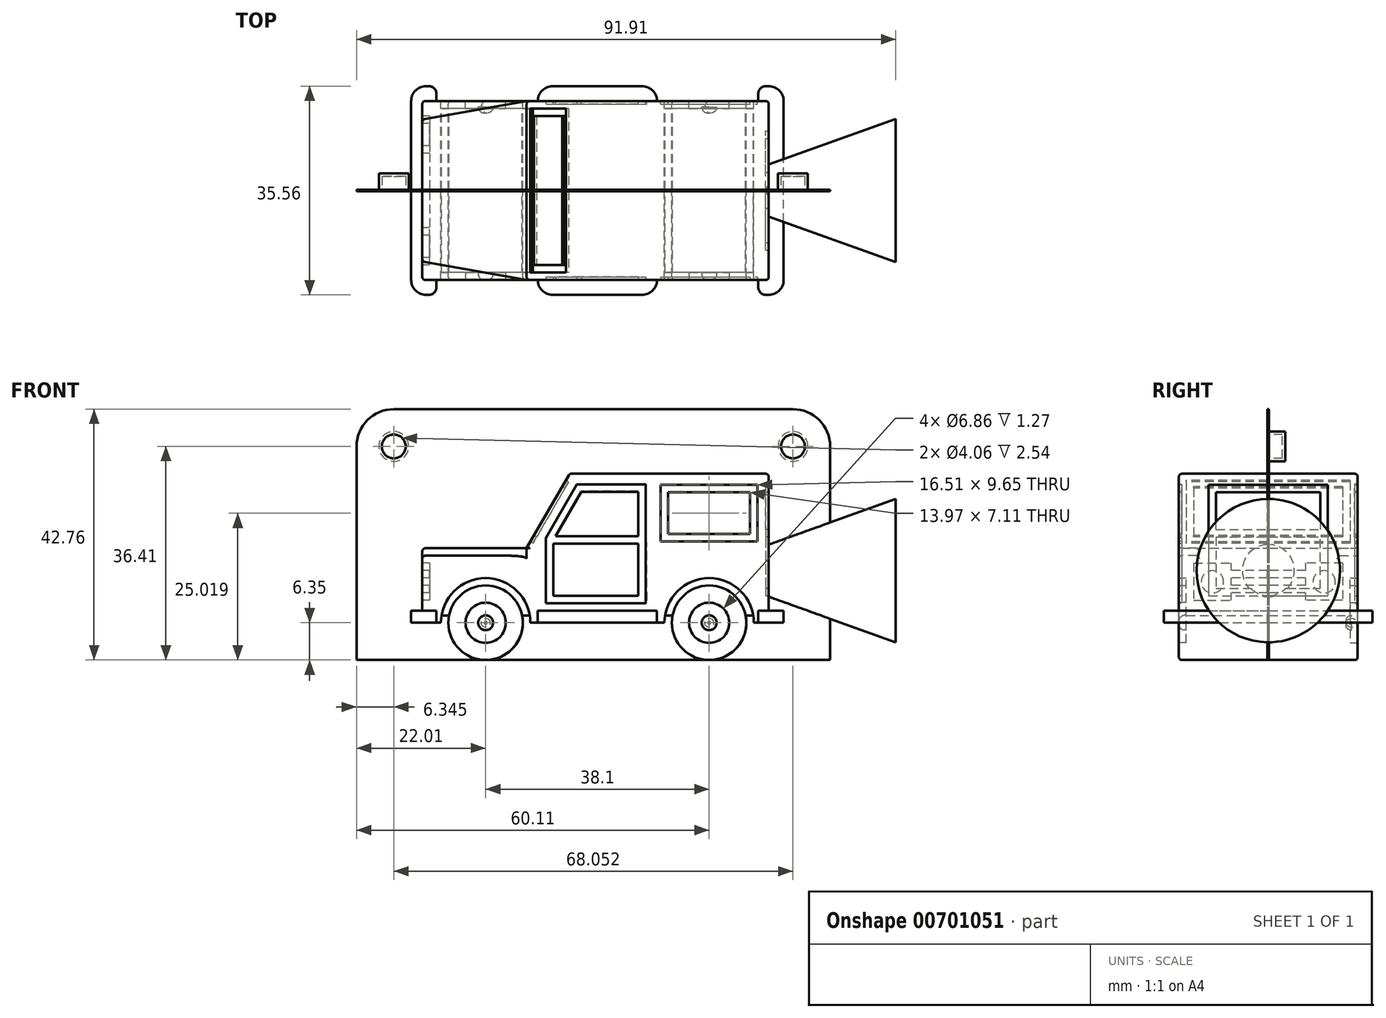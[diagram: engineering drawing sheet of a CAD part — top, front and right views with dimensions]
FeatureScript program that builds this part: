
annotation { "Feature Type Name" : "Feature", "Feature Type Description" : "" }
export const myFeature = defineFeature(function(context is Context, id is Id, definition is map)
    precondition{}
    {
        {
            var Q0;
            Q0=qCreatedBy(makeId("Front.planeOp"),FACE);
            var sketch = newSketch(context, id + "F0", { "sketchPlane" : qUnion([Q0])});
            skLineSegment(sketch, "E0", {"start": v(-29.85, 6.35) * mm, "end": v(42.48, 6.35) * mm, "construction": true});
            skPoint(sketch, "E1", {"position": v(-19.05, 6.35) * mm});
            skPoint(sketch, "E2", {"position": v(19.05, 6.35) * mm});
            skLineSegment(sketch, "E3", {"start": v(-105.53, 0) * mm, "end": v(109.36, 0) * mm, "construction": true});
            skCircle(sketch, "E4", {"center": v(-19.05, 6.35) * mm, "radius": 6.35 * mm});
            skCircle(sketch, "E5", {"center": v(19.05, 6.35) * mm, "radius": 6.35 * mm});
            skArc(sketch, "E6", {"start": v(-11.43, 6.35) * mm, "mid": v(-19.05, 13.97) * mm, "end": v(-26.67, 6.35) * mm});
            skArc(sketch, "E7", {"start": v(26.67, 6.35) * mm, "mid": v(19.05, 13.97) * mm, "end": v(11.43, 6.35) * mm});
            skLineSegment(sketch, "E8", {"start": v(-26.67, 6.35) * mm, "end": v(-29.85, 6.35) * mm});
            skLineSegment(sketch, "E9", {"start": v(-29.85, 19.05) * mm, "end": v(-12.07, 19.05) * mm});
            skLineSegment(sketch, "E10", {"start": v(-12.07, 19.05) * mm, "end": v(-4.73, 31.75) * mm});
            skLineSegment(sketch, "E11", {"start": v(-4.73, 31.75) * mm, "end": v(29.21, 31.75) * mm});
            skLineSegment(sketch, "E12", {"start": v(29.21, 31.75) * mm, "end": v(29.21, 6.35) * mm});
            skLineSegment(sketch, "E13", {"start": v(29.21, 6.35) * mm, "end": v(26.67, 6.35) * mm});
            skLineSegment(sketch, "E14", {"start": v(11.43, 6.35) * mm, "end": v(-11.43, 6.35) * mm});
            skLineSegment(sketch, "E15", {"start": v(-29.85, 19.05) * mm, "end": v(-29.85, 6.35) * mm});
            skSolve(sketch);
        }
        {
            var Q0;
            Q0=makeQuery(id+"F0.imprint","IMPRINT",FACE,{"disambiguationData":[TD([[makeQuery(id+"F0.imprint","IMPRINT",EDGE,{"derivedFrom":sQuery(id+"F0.wireOp",EDGE,"E6")}),-1.0]])]});
            var Q1;
            Q1=makeQuery(id+"F0.imprint","IMPRINT",FACE,{"disambiguationData":[TD([[makeQuery(id+"F0.imprint","IMPRINT",EDGE,{"derivedFrom":sQuery(id+"F0.wireOp",EDGE,"E4")}),1.0]])]});
            var Q2;
            Q2=makeQuery(id+"F0.imprint","IMPRINT",FACE,{"disambiguationData":[TD([[makeQuery(id+"F0.imprint","IMPRINT",EDGE,{"derivedFrom":sQuery(id+"F0.wireOp",EDGE,"E5")}),1.0]])]});
            extrude(context, id + "F1", {"entities" : qUnion([Q0, Q1, Q2]), "endBound" : BoundingType.SYMMETRIC, "depth" : 30.48 * mm, "offsetDistance" : 25.4 * mm});
        }
        {
            var Q0;
            Q0=makeQuery(id+"F1.opExtrude","SWEPT_FACE",FACE,{"disambiguationData":[OSD([sQuery(id+"F0.wireOp",EDGE,"E14")])]});
            var sketch = newSketch(context, id + "F2", { "sketchPlane" : qUnion([Q0])});
            skLineSegment(sketch, "E16.bottom", {"start": v(-7.62, 17.78) * mm, "end": v(7.62, 17.78) * mm});
            skLineSegment(sketch, "E16.top", {"start": v(-7.62, -17.78) * mm, "end": v(7.62, -17.78) * mm});
            skLineSegment(sketch, "E16.left", {"start": v(-10.16, 15.24) * mm, "end": v(-10.16, -15.24) * mm});
            skLineSegment(sketch, "E16.right", {"start": v(10.16, 15.24) * mm, "end": v(10.16, -15.24) * mm});
            skPoint(sketch, "E17.visualSharp", {"position": v(-10.16, 17.78) * mm});
            skArc(sketch, "E17.filletArc", {"start": v(-7.62, 17.78) * mm, "mid": v(-9.42, 17.04) * mm, "end": v(-10.16, 15.24) * mm});
            skPoint(sketch, "E18.visualSharp", {"position": v(10.16, 17.78) * mm});
            skArc(sketch, "E18.filletArc", {"start": v(10.16, 15.24) * mm, "mid": v(9.42, 17.04) * mm, "end": v(7.62, 17.78) * mm});
            skPoint(sketch, "E19.visualSharp", {"position": v(10.16, -17.78) * mm});
            skArc(sketch, "E19.filletArc", {"start": v(7.62, -17.78) * mm, "mid": v(9.42, -17.04) * mm, "end": v(10.16, -15.24) * mm});
            skPoint(sketch, "E20.visualSharp", {"position": v(-10.16, -17.78) * mm});
            skArc(sketch, "E20.filletArc", {"start": v(-10.16, -15.24) * mm, "mid": v(-9.42, -17.04) * mm, "end": v(-7.62, -17.78) * mm});
            skLineSegment(sketch, "E21.bottom", {"start": v(-29.21, 17.78) * mm, "end": v(-28.7, 17.78) * mm});
            skLineSegment(sketch, "E21.top", {"start": v(-29.21, -17.78) * mm, "end": v(-28.7, -17.78) * mm});
            skLineSegment(sketch, "E21.left", {"start": v(-31.75, 15.24) * mm, "end": v(-31.75, -15.24) * mm});
            skLineSegment(sketch, "E21.right", {"start": v(-27.43, 16.51) * mm, "end": v(-27.43, -16.51) * mm});
            skPoint(sketch, "E22.visualSharp", {"position": v(-31.75, 17.78) * mm});
            skArc(sketch, "E22.filletArc", {"start": v(-29.21, 17.78) * mm, "mid": v(-31, 17.04) * mm, "end": v(-31.75, 15.24) * mm});
            skPoint(sketch, "E23.visualSharp", {"position": v(-31.75, -17.78) * mm});
            skArc(sketch, "E23.filletArc", {"start": v(-31.75, -15.24) * mm, "mid": v(-31, -17.04) * mm, "end": v(-29.21, -17.78) * mm});
            skPoint(sketch, "E24.visualSharp", {"position": v(-27.43, 17.78) * mm});
            skArc(sketch, "E24.filletArc", {"start": v(-27.43, 16.51) * mm, "mid": v(-27.8, 17.4) * mm, "end": v(-28.7, 17.78) * mm});
            skPoint(sketch, "E25.visualSharp", {"position": v(-27.43, -17.78) * mm});
            skArc(sketch, "E25.filletArc", {"start": v(-28.7, -17.78) * mm, "mid": v(-27.8, -17.4) * mm, "end": v(-27.43, -16.51) * mm});
            skLineSegment(sketch, "E26.bottom", {"start": v(28.7, 17.78) * mm, "end": v(29.21, 17.78) * mm});
            skLineSegment(sketch, "E26.top", {"start": v(28.7, -17.78) * mm, "end": v(29.21, -17.78) * mm});
            skLineSegment(sketch, "E26.left", {"start": v(27.43, 16.51) * mm, "end": v(27.43, -16.51) * mm});
            skLineSegment(sketch, "E26.right", {"start": v(31.75, 15.24) * mm, "end": v(31.75, -15.24) * mm});
            skPoint(sketch, "E27.visualSharp", {"position": v(27.43, 17.78) * mm});
            skArc(sketch, "E27.filletArc", {"start": v(28.7, 17.78) * mm, "mid": v(27.8, 17.4) * mm, "end": v(27.43, 16.51) * mm});
            skPoint(sketch, "E28.visualSharp", {"position": v(27.43, -17.78) * mm});
            skArc(sketch, "E28.filletArc", {"start": v(27.43, -16.51) * mm, "mid": v(27.8, -17.4) * mm, "end": v(28.7, -17.78) * mm});
            skPoint(sketch, "E29.visualSharp", {"position": v(31.75, 17.78) * mm});
            skArc(sketch, "E29.filletArc", {"start": v(31.75, 15.24) * mm, "mid": v(31, 17.04) * mm, "end": v(29.21, 17.78) * mm});
            skPoint(sketch, "E30.visualSharp", {"position": v(31.75, -17.78) * mm});
            skArc(sketch, "E30.filletArc", {"start": v(29.21, -17.78) * mm, "mid": v(31, -17.04) * mm, "end": v(31.75, -15.24) * mm});
            skSolve(sketch);
        }
        {
            var Q0;
            Q0 = qSketchRegion(id + "F2", true);
            extrude(context, id + "F3", {"entities" : qUnion([Q0]), "operationType" : NewBodyOperationType.ADD, "oppositeDirection" : true, "depth" : 2.03 * mm, "offsetDistance" : 25.4 * mm});
        }
        {
            var Q0;
            Q0=qCreatedBy(makeId("Front.planeOp"),FACE);
            var sketch = newSketch(context, id + "F4", { "sketchPlane" : qUnion([Q0])});
            skLineSegment(sketch, "E31.bottom", {"start": v(-27.92, 16.7) * mm, "end": v(28.03, 16.7) * mm});
            skLineSegment(sketch, "E31.top", {"start": v(-27.92, 7.58) * mm, "end": v(28.03, 7.58) * mm});
            skLineSegment(sketch, "E31.left", {"start": v(-27.92, 16.7) * mm, "end": v(-27.92, 7.58) * mm});
            skLineSegment(sketch, "E31.right", {"start": v(28.03, 16.7) * mm, "end": v(28.03, 7.58) * mm});
            skSolve(sketch);
        }
        {
            var Q0;
            Q0 = qSketchRegion(id + "F4", true);
            extrude(context, id + "F5", {"entities" : qUnion([Q0]), "operationType" : NewBodyOperationType.ADD, "endBound" : BoundingType.SYMMETRIC, "depth" : 27.94 * mm, "offsetDistance" : 25.4 * mm});
        }
        {
            var Q0;
            Q0=makeQuery(id+"F1.opExtrude","SWEPT_FACE",FACE,{"disambiguationData":[OSD([sQuery(id+"F0.wireOp",EDGE,"E9")])]});
            var sketch = newSketch(context, id + "F6", { "sketchPlane" : qUnion([Q0])});
            skLineSegment(sketch, "E32", {"start": v(-53.1, 0) * mm, "end": v(61.48, 0) * mm, "construction": true});
            skLineSegment(sketch, "E33", {"start": v(-34.74, 11.24) * mm, "end": v(-12.06, 15.24) * mm});
            skLineSegment(sketch, "E34", {"start": v(-12.07, 15.24) * mm, "end": v(-14.21, 27.43) * mm});
            skLineSegment(sketch, "E35", {"start": v(-14.21, 27.43) * mm, "end": v(-40.52, 22.79) * mm});
            skLineSegment(sketch, "E36", {"start": v(-40.52, 22.79) * mm, "end": v(-34.74, 11.24) * mm});
            skLineSegment(sketch, "E37.MirrorCS", {"start": v(-40.52, -22.79) * mm, "end": v(-34.74, -11.24) * mm});
            skLineSegment(sketch, "E38.MirrorCS", {"start": v(-14.21, -27.43) * mm, "end": v(-40.52, -22.79) * mm});
            skLineSegment(sketch, "E39.MirrorCS", {"start": v(-34.74, -11.24) * mm, "end": v(-12.06, -15.24) * mm});
            skLineSegment(sketch, "E40.MirrorCS", {"start": v(-12.07, -15.24) * mm, "end": v(-14.21, -27.43) * mm});
            skSolve(sketch);
        }
        {
            var Q0;
            Q0 = qSketchRegion(id + "F6", true);
            extrude(context, id + "F7", {"entities" : qUnion([Q0]), "operationType" : NewBodyOperationType.REMOVE, "oppositeDirection" : true, "depth" : 1.27 * mm, "offsetDistance" : 25.4 * mm});
        }
        {
            var Q0;
            Q0=makeQuery(id+"F1.opExtrude","SWEPT_FACE",FACE,{"disambiguationData":[OSD([sQuery(id+"F0.wireOp",EDGE,"E15")])]});
            var sketch = newSketch(context, id + "F8", { "sketchPlane" : qUnion([Q0])});
            skLineSegment(sketch, "E41", {"start": v(0, 40.96) * mm, "end": v(0, 16.51) * mm, "construction": true});
            skLineSegment(sketch, "E42.bottom", {"start": v(-12.7, 16.51) * mm, "end": v(0, 16.51) * mm});
            skLineSegment(sketch, "E42.top", {"start": v(-12.7, 10.16) * mm, "end": v(0, 10.16) * mm});
            skLineSegment(sketch, "E42.left", {"start": v(-12.7, 16.51) * mm, "end": v(-12.7, 10.16) * mm});
            skLineSegment(sketch, "E43", {"start": v(-6.35, 16.51) * mm, "end": v(-6.35, 10.16) * mm});
            skLineSegment(sketch, "E44", {"start": v(-6.35, 15.24) * mm, "end": v(0, 15.24) * mm});
            skLineSegment(sketch, "E45", {"start": v(-6.35, 13.97) * mm, "end": v(0, 13.97) * mm});
            skLineSegment(sketch, "E46", {"start": v(-6.35, 12.7) * mm, "end": v(0, 12.7) * mm});
            skLineSegment(sketch, "E47", {"start": v(-6.35, 11.43) * mm, "end": v(0, 11.43) * mm});
            skLineSegment(sketch, "E48.trimOffspring", {"start": v(0, 15.24) * mm, "end": v(0, -15.6) * mm, "construction": true});
            skPoint(sketch, "E49", {"position": v(-9.53, 13.34) * mm});
            skCircle(sketch, "E50", {"center": v(-9.53, 13.34) * mm, "radius": 1.9 * mm});
            skLineSegment(sketch, "E51.MirrorCS", {"start": v(12.7, 10.16) * mm, "end": v(0, 10.16) * mm});
            skLineSegment(sketch, "E52.MirrorCS", {"start": v(12.7, 16.51) * mm, "end": v(12.7, 10.16) * mm});
            skLineSegment(sketch, "E53.MirrorCS", {"start": v(6.35, 15.24) * mm, "end": v(0, 15.24) * mm});
            skLineSegment(sketch, "E54.MirrorCS", {"start": v(6.35, 11.43) * mm, "end": v(0, 11.43) * mm});
            skLineSegment(sketch, "E55.MirrorCS", {"start": v(6.35, 12.7) * mm, "end": v(0, 12.7) * mm});
            skLineSegment(sketch, "E56.MirrorCS", {"start": v(6.35, 13.97) * mm, "end": v(0, 13.97) * mm});
            skLineSegment(sketch, "E57.MirrorCS", {"start": v(12.7, 16.51) * mm, "end": v(0, 16.51) * mm});
            skLineSegment(sketch, "E58.MirrorCS", {"start": v(6.35, 16.51) * mm, "end": v(6.35, 10.16) * mm});
            skPoint(sketch, "E59.MirrorP", {"position": v(9.53, 13.34) * mm});
            skCircle(sketch, "E60.MirrorC", {"center": v(9.53, 13.34) * mm, "radius": 1.9 * mm});
            skSolve(sketch);
        }
        {
            var Q0;
            {var subQ0=sQuery(id+"F8.wireOp",EDGE,"E42.left");Q0=makeQuery(id+"F8.imprint","IMPRINT",FACE,{"disambiguationData":[TD([[makeQuery(id+"F8.imprint","IMPRINT",EDGE,{"derivedFrom":subQ0}),1.0]])]});}
            var Q1;
            {var subQ4=sQuery(id+"F8.wireOp",EDGE,"E52.MirrorCS");Q1=makeQuery(id+"F8.imprint","IMPRINT",FACE,{"disambiguationData":[TD([[makeQuery(id+"F8.imprint","IMPRINT",EDGE,{"derivedFrom":subQ4}),-1.0]])]});}
            var Q2;
            {var subQ1=sQuery(id+"F8.wireOp",EDGE,"E44");Q2=makeQuery(id+"F8.imprint","IMPRINT",FACE,{"disambiguationData":[TD([[makeQuery(id+"F8.imprint","IMPRINT",EDGE,{"derivedFrom":subQ1}),-1.0]])]});}
            var Q3;
            {var subQ1=sQuery(id+"F8.wireOp",EDGE,"E46");Q3=makeQuery(id+"F8.imprint","IMPRINT",FACE,{"disambiguationData":[TD([[makeQuery(id+"F8.imprint","IMPRINT",EDGE,{"derivedFrom":subQ1}),-1.0]])]});}
            extrude(context, id + "F9", {"entities" : qUnion([Q0, Q1, Q2, Q3]), "operationType" : NewBodyOperationType.REMOVE, "oppositeDirection" : true, "depth" : 1.27 * mm, "offsetDistance" : 25.4 * mm});
        }
        {
            var Q0;
            Q0=makeQuery(id+"F1.opExtrude","SWEPT_FACE",FACE,{"disambiguationData":[OSD([sQuery(id+"F0.wireOp",EDGE,"E10")])]});
            var sketch = newSketch(context, id + "F10", { "sketchPlane" : qUnion([Q0])});
            skLineSegment(sketch, "E61.bottom", {"start": v(-13.97, 23.86) * mm, "end": v(13.97, 23.86) * mm});
            skLineSegment(sketch, "E61.top", {"start": v(-13.97, 11.74) * mm, "end": v(13.97, 11.74) * mm});
            skLineSegment(sketch, "E61.left", {"start": v(-13.97, 23.86) * mm, "end": v(-13.97, 11.74) * mm});
            skLineSegment(sketch, "E61.right", {"start": v(13.97, 23.86) * mm, "end": v(13.97, 11.74) * mm});
            skLineSegment(sketch, "E62.bottom", {"start": v(-12.7, 22.59) * mm, "end": v(12.7, 22.59) * mm});
            skLineSegment(sketch, "E62.top", {"start": v(-12.7, 13) * mm, "end": v(12.7, 13) * mm});
            skLineSegment(sketch, "E62.left", {"start": v(-12.7, 22.59) * mm, "end": v(-12.7, 13) * mm});
            skLineSegment(sketch, "E62.right", {"start": v(12.7, 22.59) * mm, "end": v(12.7, 13) * mm});
            skSolve(sketch);
        }
        {
            var Q0;
            Q0 = qSketchRegion(id + "F10", true);
            extrude(context, id + "F11", {"entities" : qUnion([Q0]), "operationType" : NewBodyOperationType.REMOVE, "oppositeDirection" : true, "depth" : 0.5 * mm, "offsetDistance" : 25.4 * mm});
        }
        {
            var Q0;
            Q0=makeQuery(id+"F1.opExtrude","CAP_FACE",FACE,{"disambiguationData":[OSD([sQuery(id+"F0.wireOp",EDGE,"E6"),sQuery(id+"F0.wireOp",EDGE,"E7"),sQuery(id+"F0.wireOp",EDGE,"E8"),sQuery(id+"F0.wireOp",EDGE,"E9"),sQuery(id+"F0.wireOp",EDGE,"E10"),sQuery(id+"F0.wireOp",EDGE,"E11"),sQuery(id+"F0.wireOp",EDGE,"E12"),sQuery(id+"F0.wireOp",EDGE,"E13"),sQuery(id+"F0.wireOp",EDGE,"E14"),sQuery(id+"F0.wireOp",EDGE,"E15")])],"isStart":false});
            var sketch = newSketch(context, id + "F12", { "sketchPlane" : qUnion([Q0])});
            skLineSegment(sketch, "E63.top", {"start": v(-8.76, 9.65) * mm, "end": v(8.25, 9.65) * mm});
            skLineSegment(sketch, "E63.left", {"start": v(-8.76, 20.82) * mm, "end": v(-8.76, 9.65) * mm});
            skLineSegment(sketch, "E63.right", {"start": v(8.25, 26.56) * mm, "end": v(8.25, 9.65) * mm});
            skLineSegment(sketch, "E64", {"start": v(-8.76, 20.82) * mm, "end": v(-3.48, 29.96) * mm});
            skLineSegment(sketch, "E65", {"start": v(-3.48, 29.96) * mm, "end": v(8.25, 29.96) * mm});
            skLineSegment(sketch, "E66", {"start": v(8.25, 29.96) * mm, "end": v(8.25, 26.56) * mm});
            skLineSegment(sketch, "E67.bottom", {"start": v(10.8, 29.84) * mm, "end": v(27.3, 29.84) * mm});
            skLineSegment(sketch, "E67.top", {"start": v(10.8, 20.2) * mm, "end": v(27.3, 20.2) * mm});
            skLineSegment(sketch, "E67.left", {"start": v(10.8, 29.84) * mm, "end": v(10.8, 20.2) * mm});
            skLineSegment(sketch, "E67.right", {"start": v(27.3, 29.85) * mm, "end": v(27.3, 20.2) * mm});
            skLineSegment(sketch, "E68.left", {"start": v(-8.76, 20.2) * mm, "end": v(-8.76, 20.2) * mm});
            skLineSegment(sketch, "E68.right", {"start": v(8.25, 20.2) * mm, "end": v(8.25, 20.2) * mm});
            skLineSegment(sketch, "E69.bottom", {"start": v(12.06, 28.57) * mm, "end": v(26.04, 28.57) * mm});
            skLineSegment(sketch, "E69.top", {"start": v(12.06, 21.46) * mm, "end": v(26.04, 21.46) * mm});
            skLineSegment(sketch, "E69.left", {"start": v(12.06, 28.57) * mm, "end": v(12.06, 21.46) * mm});
            skLineSegment(sketch, "E69.right", {"start": v(26.04, 28.58) * mm, "end": v(26.04, 21.46) * mm});
            skLineSegment(sketch, "E70", {"start": v(-2.75, 28.7) * mm, "end": v(-7.12, 21.12) * mm});
            skLineSegment(sketch, "E71", {"start": v(6.98, 21.12) * mm, "end": v(6.98, 28.7) * mm});
            skLineSegment(sketch, "E72", {"start": v(6.98, 28.7) * mm, "end": v(-2.75, 28.7) * mm});
            skLineSegment(sketch, "E73.bottom", {"start": v(-7.5, 19.85) * mm, "end": v(6.98, 19.85) * mm});
            skLineSegment(sketch, "E73.top", {"start": v(-7.5, 10.92) * mm, "end": v(6.98, 10.92) * mm});
            skLineSegment(sketch, "E73.left", {"start": v(-7.5, 19.85) * mm, "end": v(-7.5, 10.92) * mm});
            skLineSegment(sketch, "E73.right", {"start": v(6.98, 19.85) * mm, "end": v(6.98, 10.92) * mm});
            skLineSegment(sketch, "E74", {"start": v(-7.12, 21.12) * mm, "end": v(6.98, 21.12) * mm});
            skSolve(sketch);
        }
        {
            var Q0;
            Q0=makeQuery(id+"F1.opExtrude","CAP_FACE",FACE,{"disambiguationData":[OSD([sQuery(id+"F0.wireOp",EDGE,"E6"),sQuery(id+"F0.wireOp",EDGE,"E7"),sQuery(id+"F0.wireOp",EDGE,"E8"),sQuery(id+"F0.wireOp",EDGE,"E9"),sQuery(id+"F0.wireOp",EDGE,"E10"),sQuery(id+"F0.wireOp",EDGE,"E11"),sQuery(id+"F0.wireOp",EDGE,"E12"),sQuery(id+"F0.wireOp",EDGE,"E13"),sQuery(id+"F0.wireOp",EDGE,"E14"),sQuery(id+"F0.wireOp",EDGE,"E15")])],"isStart":true});
            var sketch = newSketch(context, id + "F13", { "sketchPlane" : qUnion([Q0])});
            skLineSegment(sketch, "E75.MirrorCS", {"start": v(7.5, 19.93) * mm, "end": v(7.5, 10.92) * mm});
            skLineSegment(sketch, "E76.MirrorCS", {"start": v(-6.98, 19.93) * mm, "end": v(-6.98, 10.92) * mm});
            skLineSegment(sketch, "E77.MirrorCS", {"start": v(7.12, 21.2) * mm, "end": v(-6.98, 21.2) * mm});
            skLineSegment(sketch, "E78.MirrorCS", {"start": v(8.75, 9.65) * mm, "end": v(-8.4, 9.65) * mm});
            skLineSegment(sketch, "E79.MirrorCS", {"start": v(-12.06, 28.58) * mm, "end": v(-12.06, 21.46) * mm});
            skLineSegment(sketch, "E80.MirrorCS", {"start": v(-26.03, 28.58) * mm, "end": v(-26.03, 21.46) * mm});
            skLineSegment(sketch, "E81.MirrorCS", {"start": v(2.75, 28.77) * mm, "end": v(7.12, 21.2) * mm});
            skLineSegment(sketch, "E82.MirrorCS", {"start": v(7.5, 10.92) * mm, "end": v(-6.98, 10.92) * mm});
            skLineSegment(sketch, "E83.MirrorCS", {"start": v(7.5, 19.93) * mm, "end": v(-6.98, 19.93) * mm});
            skLineSegment(sketch, "E84.MirrorCS", {"start": v(-6.98, 28.77) * mm, "end": v(2.75, 28.77) * mm});
            skLineSegment(sketch, "E85.MirrorCS", {"start": v(-6.98, 21.2) * mm, "end": v(-6.98, 28.77) * mm});
            skLineSegment(sketch, "E86.MirrorCS", {"start": v(-12.06, 21.46) * mm, "end": v(-26.03, 21.46) * mm});
            skLineSegment(sketch, "E87.MirrorCS", {"start": v(-12.06, 28.58) * mm, "end": v(-26.03, 28.58) * mm});
            skLineSegment(sketch, "E88.MirrorCS", {"start": v(-27.3, 29.85) * mm, "end": v(-27.3, 20.2) * mm});
            skLineSegment(sketch, "E89.MirrorCS", {"start": v(-10.8, 29.85) * mm, "end": v(-10.8, 20.2) * mm});
            skLineSegment(sketch, "E90.MirrorCS", {"start": v(-10.8, 20.2) * mm, "end": v(-27.3, 20.2) * mm});
            skLineSegment(sketch, "E91.MirrorCS", {"start": v(-10.8, 29.84) * mm, "end": v(-27.3, 29.84) * mm});
            skLineSegment(sketch, "E92.MirrorCS", {"start": v(8.75, 20.9) * mm, "end": v(3.47, 30.04) * mm});
            skLineSegment(sketch, "E93.MirrorCS", {"start": v(8.75, 20.9) * mm, "end": v(8.75, 9.65) * mm});
            skLineSegment(sketch, "E94.MirrorCS", {"start": v(3.47, 30.04) * mm, "end": v(-8.25, 30.04) * mm});
            skLineSegment(sketch, "E95", {"start": v(-8.25, 30.04) * mm, "end": v(-8.4, 9.65) * mm});
            skSolve(sketch);
        }
        {
            var Q0;
            Q0 = qSketchRegion(id + "F12", true);
            extrude(context, id + "F14", {"entities" : qUnion([Q0]), "operationType" : NewBodyOperationType.REMOVE, "oppositeDirection" : true, "depth" : 0.5 * mm, "offsetDistance" : 25.4 * mm});
        }
        {
            var Q0;
            Q0 = qSketchRegion(id + "F13", true);
            extrude(context, id + "F15", {"entities" : qUnion([Q0]), "operationType" : NewBodyOperationType.REMOVE, "oppositeDirection" : true, "depth" : 0.5 * mm, "offsetDistance" : 25.4 * mm});
        }
        {
            var Q0;
            Q0=makeQuery(id+"F1.opExtrude","SWEPT_FACE",FACE,{"disambiguationData":[OSD([sQuery(id+"F0.wireOp",EDGE,"E12")])]});
            var sketch = newSketch(context, id + "F16", { "sketchPlane" : qUnion([Q0])});
            skLineSegment(sketch, "E96.bottom", {"start": v(-10.16, 29.84) * mm, "end": v(10.16, 29.84) * mm});
            skLineSegment(sketch, "E96.top", {"start": v(-10.16, 10.92) * mm, "end": v(10.16, 10.92) * mm});
            skLineSegment(sketch, "E96.left", {"start": v(-10.16, 29.84) * mm, "end": v(-10.16, 10.92) * mm});
            skLineSegment(sketch, "E96.right", {"start": v(10.16, 29.84) * mm, "end": v(10.16, 10.92) * mm});
            skLineSegment(sketch, "E97", {"start": v(-8.89, 22.22) * mm, "end": v(8.89, 22.22) * mm});
            skLineSegment(sketch, "E98", {"start": v(-8.89, 20.95) * mm, "end": v(8.89, 20.95) * mm});
            skLineSegment(sketch, "E99", {"start": v(-8.89, 22.22) * mm, "end": v(-8.89, 28.57) * mm});
            skLineSegment(sketch, "E100", {"start": v(-8.89, 28.57) * mm, "end": v(8.89, 28.57) * mm});
            skLineSegment(sketch, "E101", {"start": v(8.89, 28.57) * mm, "end": v(8.89, 22.22) * mm});
            skLineSegment(sketch, "E102", {"start": v(-8.89, 20.95) * mm, "end": v(-8.89, 12.2) * mm});
            skLineSegment(sketch, "E103", {"start": v(-8.89, 12.2) * mm, "end": v(8.89, 12.2) * mm});
            skLineSegment(sketch, "E104", {"start": v(8.89, 12.2) * mm, "end": v(8.89, 20.95) * mm});
            skPoint(sketch, "E105.orphan", {"position": v(10.16, 22.22) * mm});
            skPoint(sketch, "E106.orphan", {"position": v(10.16, 20.95) * mm});
            skSolve(sketch);
        }
        {
            var Q0;
            Q0 = qSketchRegion(id + "F16", true);
            extrude(context, id + "F17", {"entities" : qUnion([Q0]), "operationType" : NewBodyOperationType.REMOVE, "oppositeDirection" : true, "depth" : 0.5 * mm, "offsetDistance" : 25.4 * mm});
        }
        {
            var Q0;
            Q0=makeQuery(id+"F1.opExtrude","CAP_FACE",FACE,{"disambiguationData":[OSD([sQuery(id+"F0.wireOp",EDGE,"E5")])],"isStart":false});
            var sketch = newSketch(context, id + "F18", { "sketchPlane" : qUnion([Q0])});
            skPoint(sketch, "E107", {"position": v(19.05, 6.35) * mm});
            skPoint(sketch, "E108", {"position": v(-19.05, 6.35) * mm});
            skCircle(sketch, "E109", {"center": v(-19.05, 6.35) * mm, "radius": 3.43 * mm});
            skCircle(sketch, "E110", {"center": v(19.05, 6.35) * mm, "radius": 3.43 * mm});
            skCircle(sketch, "E111", {"center": v(-19.05, 6.35) * mm, "radius": 1.27 * mm});
            skCircle(sketch, "E112", {"center": v(19.05, 6.35) * mm, "radius": 1.27 * mm});
            skSolve(sketch);
        }
        {
            var Q0;
            Q0=makeQuery(id+"F18.imprint","IMPRINT",FACE,{"disambiguationData":[TD([[makeQuery(id+"F18.imprint","IMPRINT",EDGE,{"derivedFrom":sQuery(id+"F18.wireOp",EDGE,"E110")}),1.0]])]});
            var Q1;
            Q1=makeQuery(id+"F18.imprint","IMPRINT",FACE,{"disambiguationData":[TD([[makeQuery(id+"F18.imprint","IMPRINT",EDGE,{"derivedFrom":sQuery(id+"F18.wireOp",EDGE,"E109")}),1.0]])]});
            extrude(context, id + "F19", {"entities" : qUnion([Q0, Q1]), "operationType" : NewBodyOperationType.REMOVE, "oppositeDirection" : true, "depth" : 1.27 * mm, "offsetDistance" : 25.4 * mm});
        }
        {
            var Q0;
            Q0=makeQuery(id+"F1.opExtrude","CAP_FACE",FACE,{"disambiguationData":[OSD([sQuery(id+"F0.wireOp",EDGE,"E5")])],"isStart":true});
            var sketch = newSketch(context, id + "F20", { "sketchPlane" : qUnion([Q0])});
            skPoint(sketch, "E113", {"position": v(-19.05, 6.35) * mm});
            skPoint(sketch, "E114", {"position": v(19.05, 6.35) * mm});
            skCircle(sketch, "E115", {"center": v(-19.05, 6.35) * mm, "radius": 3.43 * mm});
            skCircle(sketch, "E116", {"center": v(-19.05, 6.35) * mm, "radius": 1.27 * mm});
            skCircle(sketch, "E117", {"center": v(19.05, 6.35) * mm, "radius": 1.27 * mm});
            skCircle(sketch, "E118", {"center": v(19.05, 6.35) * mm, "radius": 3.43 * mm});
            skSolve(sketch);
        }
        {
            var Q0;
            Q0 = qSketchRegion(id + "F20", true);
            extrude(context, id + "F21", {"entities" : qUnion([Q0]), "operationType" : NewBodyOperationType.REMOVE, "oppositeDirection" : true, "depth" : 1.27 * mm, "offsetDistance" : 25.4 * mm});
        }
        {
            var Q0;
            Q0=makeQuery(id+"F1.opExtrude","CAP_EDGE",EDGE,{"disambiguationData":[OSD([sQuery(id+"F0.wireOp",EDGE,"E11")])],"isStart":true});
            var Q1;
            Q1=makeQuery(id+"F1.opExtrude","CAP_EDGE",EDGE,{"disambiguationData":[OSD([sQuery(id+"F0.wireOp",EDGE,"E11")])],"isStart":false});
            var Q2;
            Q2=makeQuery(id+"F1.opExtrude","SWEPT_EDGE",EDGE,{"disambiguationData":[OSD([sQuery(id+"F0.wireOp",EDGE,"E10"),sQuery(id+"F0.wireOp",EDGE,"E11")])]});
            var Q3;
            Q3=makeQuery(id+"F1.opExtrude","SWEPT_EDGE",EDGE,{"disambiguationData":[OSD([sQuery(id+"F0.wireOp",EDGE,"E11"),sQuery(id+"F0.wireOp",EDGE,"E12")])]});
            var Q4;
            Q4=makeQuery(id+"F1.opExtrude","CAP_EDGE",EDGE,{"disambiguationData":[OSD([sQuery(id+"F0.wireOp",EDGE,"E12")])],"isStart":false});
            var Q5;
            Q5=makeQuery(id+"F1.opExtrude","CAP_EDGE",EDGE,{"disambiguationData":[OSD([sQuery(id+"F0.wireOp",EDGE,"E12")])],"isStart":true});
            var Q6;
            Q6=makeQuery(id+"F1.opExtrude","CAP_EDGE",EDGE,{"disambiguationData":[OSD([sQuery(id+"F0.wireOp",EDGE,"E10")])],"isStart":false});
            var Q7;
            Q7=makeQuery(id+"F1.opExtrude","CAP_EDGE",EDGE,{"disambiguationData":[OSD([sQuery(id+"F0.wireOp",EDGE,"E10")])],"isStart":true});
            var Q8;
            Q8=makeQuery(id+"F7.boolean.opBoolean","INTERSECT",EDGE,{"derivedFrom":[makeQuery(id+"F1.opExtrude","CAP_FACE",FACE,{"disambiguationData":[OSD([sQuery(id+"F0.wireOp",EDGE,"E6"),sQuery(id+"F0.wireOp",EDGE,"E7"),sQuery(id+"F0.wireOp",EDGE,"E8"),sQuery(id+"F0.wireOp",EDGE,"E9"),sQuery(id+"F0.wireOp",EDGE,"E10"),sQuery(id+"F0.wireOp",EDGE,"E11"),sQuery(id+"F0.wireOp",EDGE,"E12"),sQuery(id+"F0.wireOp",EDGE,"E13"),sQuery(id+"F0.wireOp",EDGE,"E14"),sQuery(id+"F0.wireOp",EDGE,"E15")])],"isStart":false}),makeQuery(id+"F7.opExtrude","CAP_FACE",FACE,{"disambiguationData":[OSD([sQuery(id+"F6.wireOp",EDGE,"E37.MirrorCS"),sQuery(id+"F6.wireOp",EDGE,"E38.MirrorCS"),sQuery(id+"F6.wireOp",EDGE,"E39.MirrorCS"),sQuery(id+"F6.wireOp",EDGE,"E40.MirrorCS")])],"isStart":false})]});
            var Q9;
            Q9=makeQuery(id+"F1.opExtrude","CAP_EDGE",EDGE,{"disambiguationData":[OSD([sQuery(id+"F0.wireOp",EDGE,"E15")])],"isStart":false});
            var Q10;
            Q10=makeQuery(id+"F7.boolean.opBoolean","INTERSECT",EDGE,{"derivedFrom":[makeQuery(id+"F1.opExtrude","SWEPT_FACE",FACE,{"disambiguationData":[OSD([sQuery(id+"F0.wireOp",EDGE,"E15")])]}),makeQuery(id+"F7.opExtrude","CAP_FACE",FACE,{"disambiguationData":[OSD([sQuery(id+"F6.wireOp",EDGE,"E37.MirrorCS"),sQuery(id+"F6.wireOp",EDGE,"E38.MirrorCS"),sQuery(id+"F6.wireOp",EDGE,"E39.MirrorCS"),sQuery(id+"F6.wireOp",EDGE,"E40.MirrorCS")])],"isStart":false})]});
            var Q11;
            Q11=makeQuery(id+"F7.boolean.opBoolean","INTERSECT",EDGE,{"derivedFrom":[makeQuery(id+"F1.opExtrude","SWEPT_FACE",FACE,{"disambiguationData":[OSD([sQuery(id+"F0.wireOp",EDGE,"E15")])]}),makeQuery(id+"F7.opExtrude","SWEPT_FACE",FACE,{"disambiguationData":[OSD([sQuery(id+"F6.wireOp",EDGE,"E39.MirrorCS")])]})]});
            var Q12;
            Q12=makeQuery(id+"F1.opExtrude","SWEPT_EDGE",EDGE,{"disambiguationData":[OSD([sQuery(id+"F0.wireOp",EDGE,"E9"),sQuery(id+"F0.wireOp",EDGE,"E15")])]});
            var Q13;
            Q13=makeQuery(id+"F7.boolean.opBoolean","INTERSECT",EDGE,{"derivedFrom":[makeQuery(id+"F1.opExtrude","SWEPT_FACE",FACE,{"disambiguationData":[OSD([sQuery(id+"F0.wireOp",EDGE,"E15")])]}),makeQuery(id+"F7.opExtrude","SWEPT_FACE",FACE,{"disambiguationData":[OSD([sQuery(id+"F6.wireOp",EDGE,"E33")])]})]});
            var Q14;
            Q14=makeQuery(id+"F7.boolean.opBoolean","INTERSECT",EDGE,{"derivedFrom":[makeQuery(id+"F1.opExtrude","SWEPT_FACE",FACE,{"disambiguationData":[OSD([sQuery(id+"F0.wireOp",EDGE,"E15")])]}),makeQuery(id+"F7.opExtrude","CAP_FACE",FACE,{"disambiguationData":[OSD([sQuery(id+"F6.wireOp",EDGE,"E33"),sQuery(id+"F6.wireOp",EDGE,"E34"),sQuery(id+"F6.wireOp",EDGE,"E35"),sQuery(id+"F6.wireOp",EDGE,"E36")])],"isStart":false})]});
            var Q15;
            Q15=makeQuery(id+"F1.opExtrude","CAP_EDGE",EDGE,{"disambiguationData":[OSD([sQuery(id+"F0.wireOp",EDGE,"E15")])],"isStart":true});
            var Q16;
            Q16=makeQuery(id+"F7.boolean.opBoolean","INTERSECT",EDGE,{"derivedFrom":[makeQuery(id+"F1.opExtrude","CAP_FACE",FACE,{"disambiguationData":[OSD([sQuery(id+"F0.wireOp",EDGE,"E6"),sQuery(id+"F0.wireOp",EDGE,"E7"),sQuery(id+"F0.wireOp",EDGE,"E8"),sQuery(id+"F0.wireOp",EDGE,"E9"),sQuery(id+"F0.wireOp",EDGE,"E10"),sQuery(id+"F0.wireOp",EDGE,"E11"),sQuery(id+"F0.wireOp",EDGE,"E12"),sQuery(id+"F0.wireOp",EDGE,"E13"),sQuery(id+"F0.wireOp",EDGE,"E14"),sQuery(id+"F0.wireOp",EDGE,"E15")])],"isStart":true}),makeQuery(id+"F7.opExtrude","CAP_FACE",FACE,{"disambiguationData":[OSD([sQuery(id+"F6.wireOp",EDGE,"E33"),sQuery(id+"F6.wireOp",EDGE,"E34"),sQuery(id+"F6.wireOp",EDGE,"E35"),sQuery(id+"F6.wireOp",EDGE,"E36")])],"isStart":false})]});
            fillet(context, id + "F22", {"entities" : qUnion([Q0, Q1, Q2, Q3, Q4, Q5, Q6, Q7, Q8, Q9, Q10, Q11, Q12, Q13, Q14, Q15, Q16]), "radius" : 0.5 * mm, "tangentPropagation" : true, "allowEdgeOverflow" : false});
        }
        {
            var Q0;
            Q0=makeQuery(id+"F1.opExtrude","CAP_EDGE",EDGE,{"disambiguationData":[OSD([sQuery(id+"F0.wireOp",EDGE,"E4")])],"isStart":false});
            var Q1;
            Q1=makeQuery(id+"F1.opExtrude","CAP_EDGE",EDGE,{"disambiguationData":[OSD([sQuery(id+"F0.wireOp",EDGE,"E5")])],"isStart":false});
            var Q2;
            Q2=makeQuery(id+"F19.boolean.opBoolean","COPY",EDGE,{"derivedFrom":makeQuery(id+"F19.opExtrude","CAP_EDGE",EDGE,{"disambiguationData":[OSD([sQuery(id+"F18.wireOp",EDGE,"E109")])],"isStart":true})});
            var Q3;
            Q3=makeQuery(id+"F19.boolean.opBoolean","COPY",EDGE,{"derivedFrom":makeQuery(id+"F19.opExtrude","CAP_EDGE",EDGE,{"disambiguationData":[OSD([sQuery(id+"F18.wireOp",EDGE,"E110")])],"isStart":true})});
            var Q4;
            Q4=makeQuery(id+"F21.boolean.opBoolean","COPY",EDGE,{"derivedFrom":makeQuery(id+"F21.opExtrude","CAP_EDGE",EDGE,{"disambiguationData":[OSD([sQuery(id+"F20.wireOp",EDGE,"E115")])],"isStart":true})});
            var Q5;
            Q5=makeQuery(id+"F1.opExtrude","CAP_EDGE",EDGE,{"disambiguationData":[OSD([sQuery(id+"F0.wireOp",EDGE,"E5")])],"isStart":true});
            var Q6;
            Q6=makeQuery(id+"F21.boolean.opBoolean","COPY",EDGE,{"derivedFrom":makeQuery(id+"F21.opExtrude","CAP_EDGE",EDGE,{"disambiguationData":[OSD([sQuery(id+"F20.wireOp",EDGE,"E118")])],"isStart":true})});
            var Q7;
            Q7=makeQuery(id+"F1.opExtrude","CAP_EDGE",EDGE,{"disambiguationData":[OSD([sQuery(id+"F0.wireOp",EDGE,"E4")])],"isStart":true});
            fillet(context, id + "F23", {"entities" : qUnion([Q0, Q1, Q2, Q3, Q4, Q5, Q6, Q7]), "radius" : 0.5 * mm, "tangentPropagation" : true, "allowEdgeOverflow" : false});
        }
        {
            var Q0;
            Q0=makeQuery(id+"F21.boolean.opBoolean","COPY",EDGE,{"derivedFrom":makeQuery(id+"F21.opExtrude","CAP_EDGE",EDGE,{"disambiguationData":[OSD([sQuery(id+"F20.wireOp",EDGE,"E116")])],"isStart":true})});
            var Q1;
            Q1=makeQuery(id+"F21.boolean.opBoolean","COPY",EDGE,{"derivedFrom":makeQuery(id+"F21.opExtrude","CAP_EDGE",EDGE,{"disambiguationData":[OSD([sQuery(id+"F20.wireOp",EDGE,"E117")])],"isStart":true})});
            var Q2;
            Q2=makeQuery(id+"F19.boolean.opBoolean","COPY",EDGE,{"derivedFrom":makeQuery(id+"F19.opExtrude","CAP_EDGE",EDGE,{"disambiguationData":[OSD([sQuery(id+"F18.wireOp",EDGE,"E111")])],"isStart":true})});
            var Q3;
            Q3=makeQuery(id+"F19.boolean.opBoolean","COPY",EDGE,{"derivedFrom":makeQuery(id+"F19.opExtrude","CAP_EDGE",EDGE,{"disambiguationData":[OSD([sQuery(id+"F18.wireOp",EDGE,"E112")])],"isStart":true})});
            fillet(context, id + "F24", {"entities" : qUnion([Q0, Q1, Q2, Q3]), "radius" : 1.02 * mm, "tangentPropagation" : true, "allowEdgeOverflow" : false});
        }
        {
            var Q0;
            Q0=qCreatedBy(makeId("Front.planeOp"),FACE);
            var sketch = newSketch(context, id + "F25", { "sketchPlane" : qUnion([Q0])});
            skLineSegment(sketch, "E119.bottom", {"start": v(-34.71, 42.76) * mm, "end": v(33.34, 42.76) * mm});
            skLineSegment(sketch, "E119.top", {"start": v(-41.06, 0) * mm, "end": v(39.69, 0) * mm});
            skLineSegment(sketch, "E119.left", {"start": v(-41.06, 36.41) * mm, "end": v(-41.06, 0) * mm});
            skLineSegment(sketch, "E119.right", {"start": v(39.69, 36.41) * mm, "end": v(39.69, 0) * mm});
            skPoint(sketch, "E120.visualSharp", {"position": v(-41.06, 42.76) * mm});
            skArc(sketch, "E120.filletArc", {"start": v(-34.71, 42.76) * mm, "mid": v(-39.2, 40.9) * mm, "end": v(-41.06, 36.41) * mm});
            skPoint(sketch, "E121.visualSharp", {"position": v(39.69, 42.76) * mm});
            skArc(sketch, "E121.filletArc", {"start": v(39.69, 36.41) * mm, "mid": v(37.83, 40.9) * mm, "end": v(33.34, 42.76) * mm});
            skSolve(sketch);
        }
        {
            var Q0;
            Q0 = qSketchRegion(id + "F25", true);
            extrude(context, id + "F26", {"entities" : qUnion([Q0]), "operationType" : NewBodyOperationType.ADD, "endBound" : BoundingType.SYMMETRIC, "depth" : 0.25 * mm, "offsetDistance" : 25.4 * mm});
        }
        {
            var Q0;
            {var subQ8=sQuery(id+"F25.wireOp",EDGE,"E119.top");var subQ40=sQuery(id+"F25.wireOp",EDGE,"E119.bottom");var subQ41=sQuery(id+"F25.wireOp",EDGE,"E121.filletArc");var subQ42=sQuery(id+"F25.wireOp",EDGE,"E120.filletArc");var subQ43=sQuery(id+"F25.wireOp",EDGE,"E119.right");var subQ44=sQuery(id+"F25.wireOp",EDGE,"E119.left");var subQ45=makeQuery(id+"F26.opExtrude","CAP_FACE",FACE,{"disambiguationData":[OSD([subQ40,subQ8,subQ44,subQ43,subQ42,subQ41])],"isStart":false});Q0=makeQuery(id+"F26.boolean.opBoolean","SPLIT",FACE,{"disambiguationData":[TD([makeQuery(id+"F1.opExtrude","SWEPT_FACE",FACE,{"disambiguationData":[OSD([sQuery(id+"F0.wireOp",EDGE,"E8")])]})])],"derivedFrom":subQ45});}
            var sketch = newSketch(context, id + "F27", { "sketchPlane" : qUnion([Q0])});
            skCircle(sketch, "E122", {"center": v(33.34, 36.41) * mm, "radius": 2.54 * mm});
            skCircle(sketch, "E123", {"center": v(-34.71, 36.41) * mm, "radius": 2.54 * mm});
            skSolve(sketch);
        }
        {
            var Q0;
            Q0 = qSketchRegion(id + "F27", true);
            extrude(context, id + "F28", {"entities" : qUnion([Q0]), "operationType" : NewBodyOperationType.ADD, "oppositeDirection" : true, "depth" : 3.05 * mm, "offsetDistance" : 25.4 * mm});
        }
        {
            var Q0;
            {var subQ8=sQuery(id+"F25.wireOp",EDGE,"E119.top");var subQ40=sQuery(id+"F25.wireOp",EDGE,"E119.bottom");var subQ41=sQuery(id+"F25.wireOp",EDGE,"E121.filletArc");var subQ42=sQuery(id+"F25.wireOp",EDGE,"E120.filletArc");var subQ43=sQuery(id+"F25.wireOp",EDGE,"E119.right");var subQ44=sQuery(id+"F25.wireOp",EDGE,"E119.left");var subQ45=makeQuery(id+"F26.opExtrude","CAP_FACE",FACE,{"disambiguationData":[OSD([subQ40,subQ8,subQ44,subQ43,subQ42,subQ41])],"isStart":false});Q0=makeQuery(id+"F26.boolean.opBoolean","SPLIT",FACE,{"disambiguationData":[TD([makeQuery(id+"F1.opExtrude","SWEPT_FACE",FACE,{"disambiguationData":[OSD([sQuery(id+"F0.wireOp",EDGE,"E8")])]})])],"derivedFrom":subQ45});}
            var sketch = newSketch(context, id + "F29", { "sketchPlane" : qUnion([Q0])});
            skCircle(sketch, "E124", {"center": v(-34.71, 36.41) * mm, "radius": 2.03 * mm});
            skCircle(sketch, "E125", {"center": v(33.34, 36.41) * mm, "radius": 2.03 * mm});
            skSolve(sketch);
        }
        {
            var Q0;
            Q0 = qSketchRegion(id + "F29", true);
            extrude(context, id + "F30", {"entities" : qUnion([Q0]), "operationType" : NewBodyOperationType.REMOVE, "oppositeDirection" : true, "depth" : 2.54 * mm, "offsetDistance" : 25.4 * mm});
        }
        {
            var Q0;
            Q0=qCreatedBy(makeId("Front.planeOp"),FACE);
            var sketch = newSketch(context, id + "F31", { "sketchPlane" : qUnion([Q0])});
            skLineSegment(sketch, "E126", {"start": v(23.11, 15.24) * mm, "end": v(83.1, 15.24) * mm, "construction": true});
            skLineSegment(sketch, "E127", {"start": v(23.4, 17.6) * mm, "end": v(50.85, 27.46) * mm});
            skLineSegment(sketch, "E128", {"start": v(23.4, 17.6) * mm, "end": v(23.11, 15.24) * mm});
            skLineSegment(sketch, "E129", {"start": v(50.85, 27.46) * mm, "end": v(50.85, 15.24) * mm});
            skLineSegment(sketch, "E130", {"start": v(50.85, 15.24) * mm, "end": v(23.11, 15.24) * mm});
            skSolve(sketch);
        }
        {
            var Q0;
            Q0 = qSketchRegion(id + "F31", true);
            var Q1;
            Q1=sQuery(id+"F31.wireOp",EDGE,"E126");
            revolve(context, id + "F32", {"operationType" : NewBodyOperationType.ADD, "entities" : qUnion([Q0]), "axis" : qUnion([Q1]), "revolveType" : RevolveType.FULL});
        }
    });
